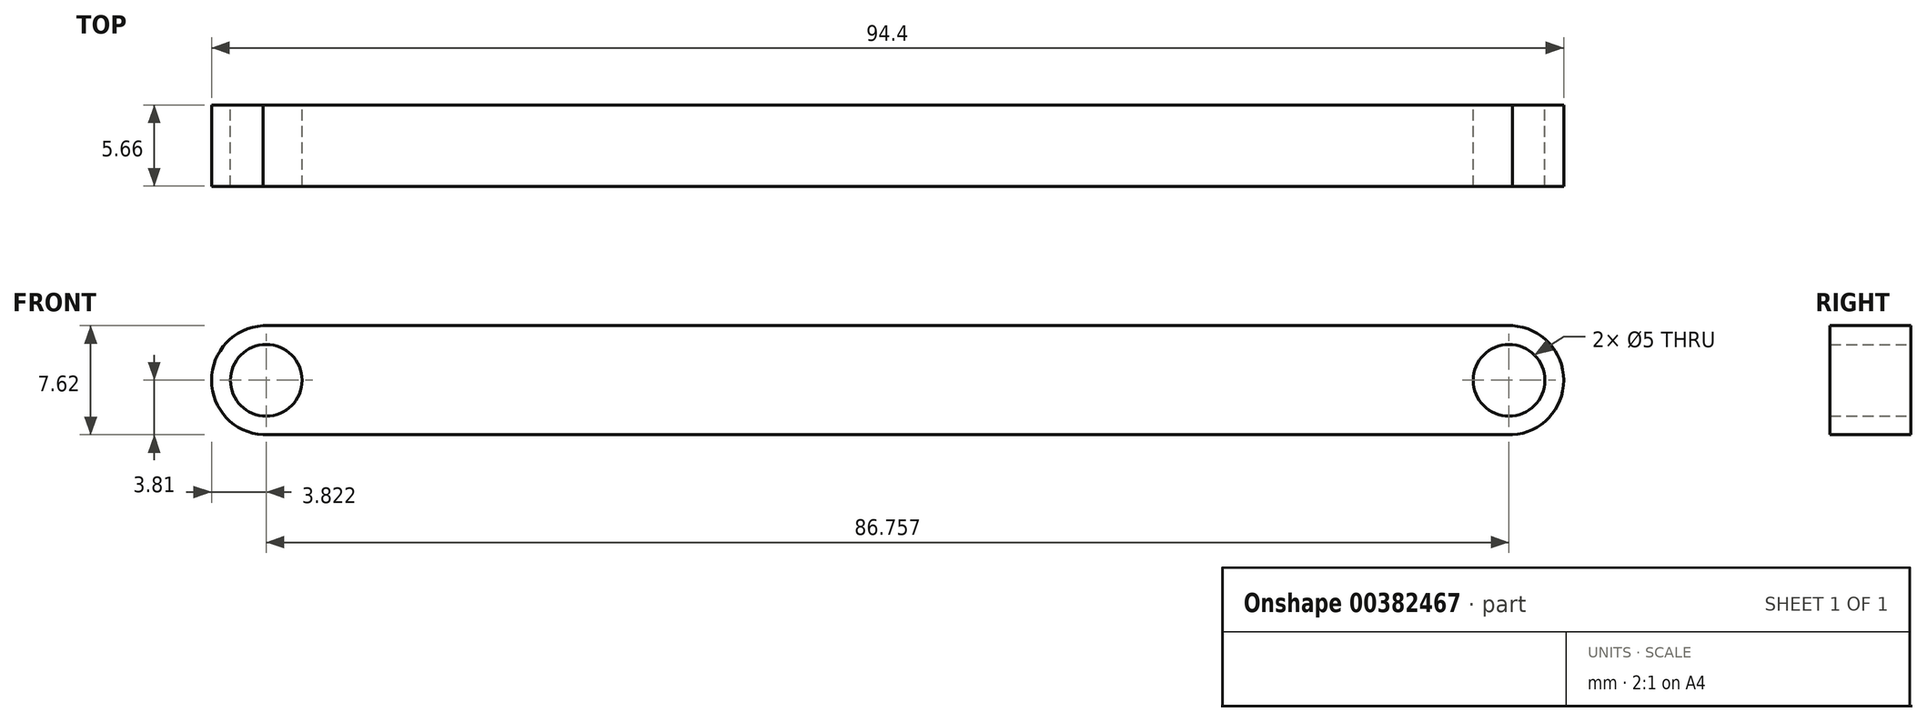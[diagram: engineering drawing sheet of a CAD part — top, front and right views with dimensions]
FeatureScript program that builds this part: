
annotation { "Feature Type Name" : "Feature", "Feature Type Description" : "" }
export const myFeature = defineFeature(function(context is Context, id is Id, definition is map)
    precondition{}
    {
        {
            var Q0;
            Q0=qCreatedBy(makeId("Front.planeOp"),FACE);
            var sketch = newSketch(context, id + "F0", { "sketchPlane" : qUnion([Q0])});
            skLineSegment(sketch, "E0.bottom", {"start": v(43.84, -3.8) * mm, "end": v(-43.38, -3.81) * mm});
            skLineSegment(sketch, "E0.top", {"start": v(43.84, 3.81) * mm, "end": v(-43.38, 3.8) * mm});
            skPoint(sketch, "E0.middle", {"position": v(0, 0) * mm});
            skCircle(sketch, "E1", {"center": v(-43.15, 0) * mm, "radius": 2.5 * mm});
            skCircle(sketch, "E2", {"center": v(43.6, 0) * mm, "radius": 2.5 * mm});
            skArc(sketch, "E3", {"start": v(-42.92, 3.8) * mm, "mid": v(-46.97, 0) * mm, "end": v(-42.92, -3.81) * mm});
            skArc(sketch, "E4", {"start": v(43.38, -3.8) * mm, "mid": v(47.43, 0) * mm, "end": v(43.38, 3.81) * mm});
            skPoint(sketch, "E0.right.end.orphan", {"position": v(-47.46, 3.8) * mm});
            skPoint(sketch, "E5.orphan", {"position": v(-47.46, -3.81) * mm});
            skPoint(sketch, "E0.left.end.orphan", {"position": v(47.46, 3.81) * mm});
            skPoint(sketch, "E6.orphan", {"position": v(47.46, -3.8) * mm});
            skSolve(sketch);
        }
        {
            var Q0;
            Q0=makeQuery(id+"F0.imprint","IMPRINT",FACE,{"disambiguationData":[TD([[makeQuery(id+"F0.imprint","IMPRINT",EDGE,{"derivedFrom":sQuery(id+"F0.wireOp",EDGE,"E1")}),-1.0]])]});
            extrude(context, id + "F1", {"entities" : qUnion([Q0]), "depth" : 5.66 * mm});
        }
    });
